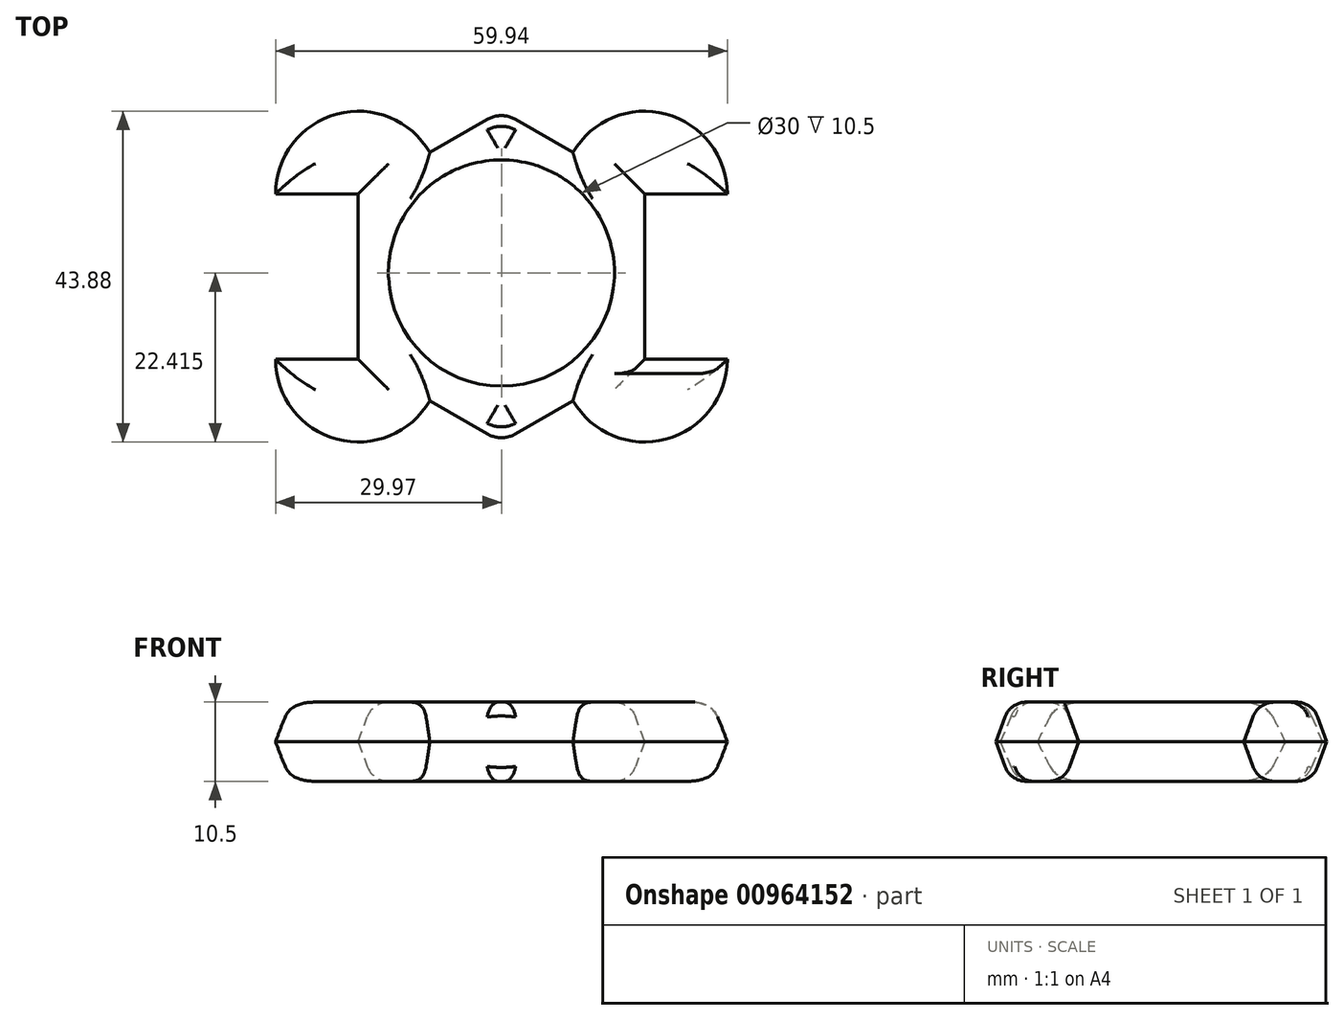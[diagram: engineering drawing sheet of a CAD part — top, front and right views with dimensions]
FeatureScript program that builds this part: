
annotation { "Feature Type Name" : "Feature", "Feature Type Description" : "" }
export const myFeature = defineFeature(function(context is Context, id is Id, definition is map)
    precondition{}
    {
        {
            var Q0;
            Q0=qCreatedBy(makeId("Top.planeOp"),FACE);
            var sketch = newSketch(context, id + "F0", { "sketchPlane" : qUnion([Q0])});
            skCircle(sketch, "E0.cCircle", {"center": v(0, 0) * mm, "radius": 19 * mm, "construction": true});
            skLineSegment(sketch, "E0.0", {"start": v(19, 10.97) * mm, "end": v(19, -10.97) * mm});
            skLineSegment(sketch, "E0.1", {"start": v(19, -10.97) * mm, "end": v(0, -21.94) * mm});
            skLineSegment(sketch, "E0.2", {"start": v(0, -21.94) * mm, "end": v(-19, -10.97) * mm});
            skLineSegment(sketch, "E0.3", {"start": v(-19, -10.97) * mm, "end": v(-19, 10.97) * mm});
            skLineSegment(sketch, "E0.4", {"start": v(-19, 10.97) * mm, "end": v(0, 21.94) * mm});
            skLineSegment(sketch, "E0.5", {"start": v(0, 21.94) * mm, "end": v(19, 10.97) * mm});
            skPoint(sketch, "E0.0.midPoint", {"position": v(19, 0) * mm});
            skArc(sketch, "E1", {"start": v(-9.5, 16.45) * mm, "mid": v(-21.84, 21.57) * mm, "end": v(-29.97, 10.97) * mm});
            skLineSegment(sketch, "E2", {"start": v(-19, 10.97) * mm, "end": v(-33.9, 10.97) * mm});
            skLineSegment(sketch, "E3.MirrorCS", {"start": v(-19, -10.97) * mm, "end": v(-33.9, -10.97) * mm});
            skArc(sketch, "E4.MirrorCS", {"start": v(-9.5, -16.45) * mm, "mid": v(-21.84, -21.57) * mm, "end": v(-29.97, -10.97) * mm});
            skArc(sketch, "E5.MirrorCS", {"start": v(9.5, 16.45) * mm, "mid": v(21.84, 21.57) * mm, "end": v(29.97, 10.97) * mm});
            skLineSegment(sketch, "E6.MirrorCS", {"start": v(19, 10.97) * mm, "end": v(33.9, 10.97) * mm});
            skArc(sketch, "E7.MirrorCS", {"start": v(9.5, -16.45) * mm, "mid": v(21.84, -21.57) * mm, "end": v(29.97, -10.97) * mm});
            skLineSegment(sketch, "E8.MirrorCS", {"start": v(19, -10.97) * mm, "end": v(33.9, -10.97) * mm});
            skSolve(sketch);
        }
        {
            var Q0;
            Q0 = qSketchRegion(id + "F0", true);
            extrude(context, id + "F1", {"entities" : qUnion([Q0]), "endBound" : BoundingType.SYMMETRIC, "depth" : 10.5 * mm, "offsetDistance" : 25 * mm, "hasDraft" : true, "draftAngle" : 20 * degree, "draftPullDirection" : true});
        }
        {
            var Q0;
            Q0=makeQuery(id+"F1.opExtrude","CAP_FACE",FACE,{"disambiguationData":[OSD([sQuery(id+"F0.wireOp",EDGE,"E0.0"),sQuery(id+"F0.wireOp",EDGE,"E0.1"),sQuery(id+"F0.wireOp",EDGE,"E0.2"),sQuery(id+"F0.wireOp",EDGE,"E0.3"),sQuery(id+"F0.wireOp",EDGE,"E0.4"),sQuery(id+"F0.wireOp",EDGE,"E0.5"),sQuery(id+"F0.wireOp",EDGE,"E1"),sQuery(id+"F0.wireOp",EDGE,"E2"),sQuery(id+"F0.wireOp",EDGE,"E3.MirrorCS"),sQuery(id+"F0.wireOp",EDGE,"E4.MirrorCS"),sQuery(id+"F0.wireOp",EDGE,"E5.MirrorCS"),sQuery(id+"F0.wireOp",EDGE,"E6.MirrorCS"),sQuery(id+"F0.wireOp",EDGE,"E7.MirrorCS"),sQuery(id+"F0.wireOp",EDGE,"E8.MirrorCS")])],"isStart":false});
            var sketch = newSketch(context, id + "F2", { "sketchPlane" : qUnion([Q0])});
            skCircle(sketch, "E9", {"center": v(0, 0.47) * mm, "radius": 15 * mm});
            skSolve(sketch);
        }
        {
            var Q0;
            Q0 = qSketchRegion(id + "F2", true);
            var Q1;
            Q1=makeQuery(id+"F2.imprint","IMPRINT",FACE,{"disambiguationData":[TD([[makeQuery(id+"F2.imprint","IMPRINT",EDGE,{"derivedFrom":sQuery(id+"F2.wireOp",EDGE,"E9")}),1.0]])]});
            extrude(context, id + "F3", {"entities" : qUnion([Q0, Q1]), "operationType" : NewBodyOperationType.REMOVE, "oppositeDirection" : true, "depth" : 25 * mm, "offsetDistance" : 25 * mm});
        }
        {
            var Q0;
            Q0=makeQuery(id+"F1.opExtrude","CAP_EDGE",EDGE,{"disambiguationData":[OSD([sQuery(id+"F0.wireOp",EDGE,"E4.MirrorCS")])],"isStart":false});
            var Q1;
            Q1=makeQuery(id+"F1.opExtrude","CAP_EDGE",EDGE,{"disambiguationData":[OSD([sQuery(id+"F0.wireOp",EDGE,"E0.2")])],"isStart":false});
            var Q2;
            Q2=makeQuery(id+"F1.opExtrude","CAP_EDGE",EDGE,{"disambiguationData":[OSD([sQuery(id+"F0.wireOp",EDGE,"E0.1")])],"isStart":false});
            var Q3;
            Q3=makeQuery(id+"F1.opExtrude","CAP_EDGE",EDGE,{"disambiguationData":[OSD([sQuery(id+"F0.wireOp",EDGE,"E7.MirrorCS")])],"isStart":false});
            var Q4;
            Q4=makeQuery(id+"F1.opExtrude","CAP_EDGE",EDGE,{"disambiguationData":[OSD([sQuery(id+"F0.wireOp",EDGE,"E0.0")])],"isStart":false});
            var Q5;
            Q5=makeQuery(id+"F1.opExtrude","CAP_EDGE",EDGE,{"disambiguationData":[OSD([sQuery(id+"F0.wireOp",EDGE,"E6.MirrorCS")])],"isStart":false});
            var Q6;
            Q6=makeQuery(id+"F1.opExtrude","CAP_EDGE",EDGE,{"disambiguationData":[OSD([sQuery(id+"F0.wireOp",EDGE,"E5.MirrorCS")])],"isStart":false});
            var Q7;
            Q7=makeQuery(id+"F1.opExtrude","CAP_EDGE",EDGE,{"disambiguationData":[OSD([sQuery(id+"F0.wireOp",EDGE,"E0.5")])],"isStart":false});
            var Q8;
            Q8=makeQuery(id+"F1.opExtrude","CAP_EDGE",EDGE,{"disambiguationData":[OSD([sQuery(id+"F0.wireOp",EDGE,"E0.4")])],"isStart":false});
            var Q9;
            Q9=makeQuery(id+"F1.opExtrude","CAP_EDGE",EDGE,{"disambiguationData":[OSD([sQuery(id+"F0.wireOp",EDGE,"E2")])],"isStart":false});
            var Q10;
            Q10=makeQuery(id+"F1.opExtrude","CAP_EDGE",EDGE,{"disambiguationData":[OSD([sQuery(id+"F0.wireOp",EDGE,"E0.3")])],"isStart":false});
            var Q11;
            Q11=makeQuery(id+"F1.opExtrude","CAP_EDGE",EDGE,{"disambiguationData":[OSD([sQuery(id+"F0.wireOp",EDGE,"E3.MirrorCS")])],"isStart":false});
            var Q12;
            Q12=makeQuery(id+"F1.opExtrude","CAP_EDGE",EDGE,{"disambiguationData":[OSD([sQuery(id+"F0.wireOp",EDGE,"E1")])],"isStart":false});
            var Q13;
            Q13=makeQuery(id+"F1.opExtrude","CAP_EDGE",EDGE,{"disambiguationData":[OSD([sQuery(id+"F0.wireOp",EDGE,"E0.1")])],"isStart":true});
            var Q14;
            Q14=makeQuery(id+"F1.opExtrude","CAP_EDGE",EDGE,{"disambiguationData":[OSD([sQuery(id+"F0.wireOp",EDGE,"E0.2")])],"isStart":true});
            var Q15;
            Q15=makeQuery(id+"F1.opExtrude","CAP_EDGE",EDGE,{"disambiguationData":[OSD([sQuery(id+"F0.wireOp",EDGE,"E7.MirrorCS")])],"isStart":true});
            var Q16;
            Q16=makeQuery(id+"F1.opExtrude","CAP_EDGE",EDGE,{"disambiguationData":[OSD([sQuery(id+"F0.wireOp",EDGE,"E8.MirrorCS")])],"isStart":true});
            var Q17;
            Q17=makeQuery(id+"F1.opExtrude","CAP_EDGE",EDGE,{"disambiguationData":[OSD([sQuery(id+"F0.wireOp",EDGE,"E0.0")])],"isStart":true});
            var Q18;
            Q18=makeQuery(id+"F1.opExtrude","CAP_EDGE",EDGE,{"disambiguationData":[OSD([sQuery(id+"F0.wireOp",EDGE,"E6.MirrorCS")])],"isStart":true});
            var Q19;
            Q19=makeQuery(id+"F1.opExtrude","CAP_EDGE",EDGE,{"disambiguationData":[OSD([sQuery(id+"F0.wireOp",EDGE,"E5.MirrorCS")])],"isStart":true});
            var Q20;
            Q20=makeQuery(id+"F1.opExtrude","CAP_EDGE",EDGE,{"disambiguationData":[OSD([sQuery(id+"F0.wireOp",EDGE,"E0.5")])],"isStart":true});
            var Q21;
            Q21=makeQuery(id+"F1.opExtrude","CAP_EDGE",EDGE,{"disambiguationData":[OSD([sQuery(id+"F0.wireOp",EDGE,"E0.4")])],"isStart":true});
            var Q22;
            Q22=makeQuery(id+"F1.opExtrude","CAP_EDGE",EDGE,{"disambiguationData":[OSD([sQuery(id+"F0.wireOp",EDGE,"E1")])],"isStart":true});
            var Q23;
            Q23=makeQuery(id+"F1.opExtrude","CAP_EDGE",EDGE,{"disambiguationData":[OSD([sQuery(id+"F0.wireOp",EDGE,"E2")])],"isStart":true});
            var Q24;
            Q24=makeQuery(id+"F1.opExtrude","CAP_EDGE",EDGE,{"disambiguationData":[OSD([sQuery(id+"F0.wireOp",EDGE,"E0.3")])],"isStart":true});
            var Q25;
            Q25=makeQuery(id+"F1.opExtrude","CAP_EDGE",EDGE,{"disambiguationData":[OSD([sQuery(id+"F0.wireOp",EDGE,"E3.MirrorCS")])],"isStart":true});
            var Q26;
            Q26=makeQuery(id+"F1.opExtrude","CAP_EDGE",EDGE,{"disambiguationData":[OSD([sQuery(id+"F0.wireOp",EDGE,"E4.MirrorCS")])],"isStart":true});
            fillet(context, id + "F4", {"entities" : qUnion([Q0, Q1, Q2, Q3, Q4, Q5, Q6, Q7, Q8, Q9, Q10, Q11, Q12, Q13, Q14, Q15, Q16, Q17, Q18, Q19, Q20, Q21, Q22, Q23, Q24, Q25, Q26]), "radius" : 3 * mm, "tangentPropagation" : true, "allowEdgeOverflow" : false});
        }
        {
            var Q0;
            Q0=makeQuery(id+"F1.*.split.splitOp","SPLIT",EDGE,{"derivedFrom":makeQuery(id+"F1.opExtrude","SWEPT_EDGE",EDGE,{"disambiguationData":[OSD([sQuery(id+"F0.wireOp",EDGE,"E0.4"),sQuery(id+"F0.wireOp",EDGE,"E0.5")])]}),"isFromBackBody":true});
            var Q1;
            Q1=makeQuery(id+"F1.*.split.splitOp","SPLIT",EDGE,{"derivedFrom":makeQuery(id+"F1.opExtrude","SWEPT_EDGE",EDGE,{"disambiguationData":[OSD([sQuery(id+"F0.wireOp",EDGE,"E0.4"),sQuery(id+"F0.wireOp",EDGE,"E0.5")])]})});
            var Q2;
            Q2=makeQuery(id+"F1.*.split.splitOp","SPLIT",EDGE,{"derivedFrom":makeQuery(id+"F1.opExtrude","SWEPT_EDGE",EDGE,{"disambiguationData":[OSD([sQuery(id+"F0.wireOp",EDGE,"E0.1"),sQuery(id+"F0.wireOp",EDGE,"E0.2")])]}),"isFromBackBody":true});
            var Q3;
            Q3=makeQuery(id+"F1.*.split.splitOp","SPLIT",EDGE,{"derivedFrom":makeQuery(id+"F1.opExtrude","SWEPT_EDGE",EDGE,{"disambiguationData":[OSD([sQuery(id+"F0.wireOp",EDGE,"E0.1"),sQuery(id+"F0.wireOp",EDGE,"E0.2")])]})});
            fillet(context, id + "F5", {"entities" : qUnion([Q0, Q1, Q2, Q3]), "radius" : 4 * mm, "tangentPropagation" : true, "allowEdgeOverflow" : false});
        }
    });
